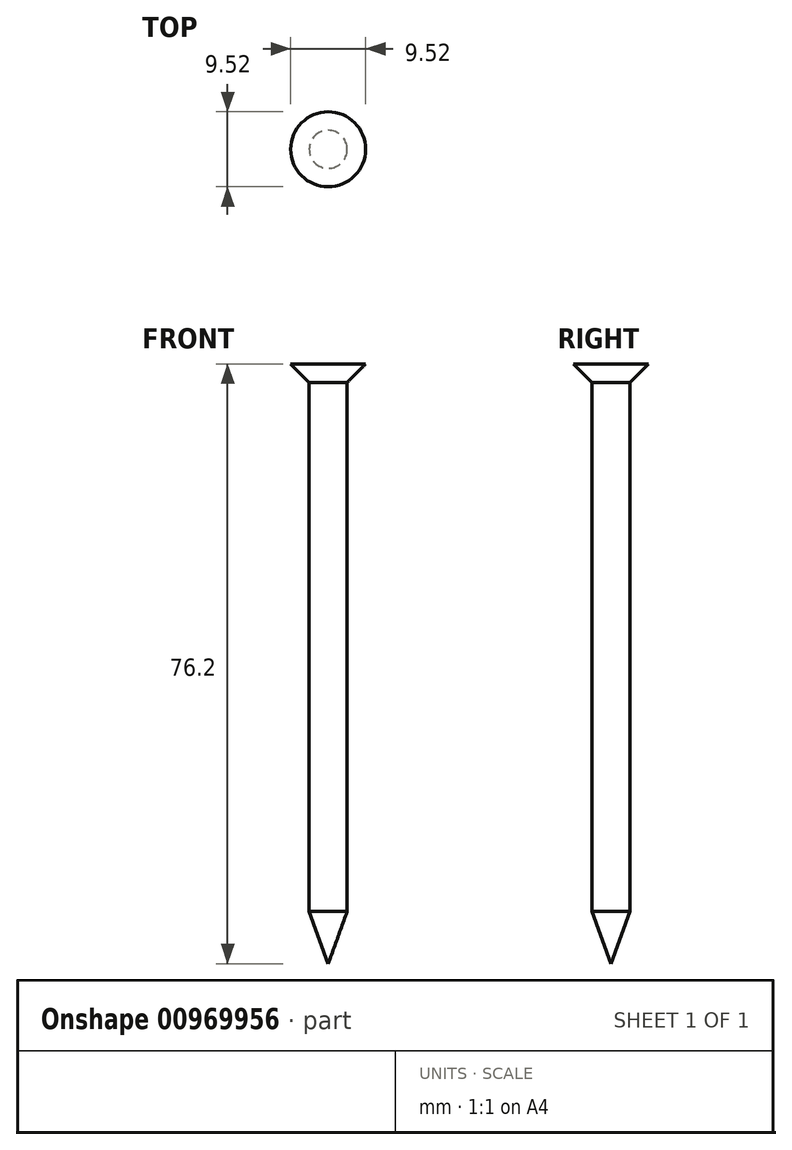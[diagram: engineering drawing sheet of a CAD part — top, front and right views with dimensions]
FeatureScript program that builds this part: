
annotation { "Feature Type Name" : "Feature", "Feature Type Description" : "" }
export const myFeature = defineFeature(function(context is Context, id is Id, definition is map)
    precondition{}
    {
        {
            var Q0;
            Q0=qCreatedBy(makeId("Front.planeOp"),FACE);
            var sketch = newSketch(context, id + "F0", { "sketchPlane" : qUnion([Q0])});
            skLineSegment(sketch, "E0", {"start": v(0, 56.88) * mm, "end": v(0, -89.13) * mm});
            skSolve(sketch);
        }
        {
            var Q0;
            Q0=qCreatedBy(makeId("Front.planeOp"),FACE);
            var sketch = newSketch(context, id + "F1", { "sketchPlane" : qUnion([Q0])});
            skLineSegment(sketch, "E1", {"start": v(0, 0) * mm, "end": v(4.76, 0) * mm});
            skLineSegment(sketch, "E2", {"start": v(4.76, 0) * mm, "end": v(2.41, -2.35) * mm});
            skLineSegment(sketch, "E3", {"start": v(2.41, -2.35) * mm, "end": v(2.41, -69.57) * mm});
            skLineSegment(sketch, "E4", {"start": v(2.41, -69.57) * mm, "end": v(0, -76.2) * mm});
            skLineSegment(sketch, "E5", {"start": v(0, -76.2) * mm, "end": v(0, 0) * mm});
            skSolve(sketch);
        }
        {
            var Q0;
            Q0 = qSketchRegion(id + "F1", true);
            var Q1;
            Q1=sQuery(id+"F0.wireOp",EDGE,"E0");
            revolve(context, id + "F2", {"surfaceOperationType" : NewSurfaceOperationType.NEW, "entities" : qUnion([Q0]), "axis" : qUnion([Q1]), "revolveType" : RevolveType.FULL});
        }
    });
